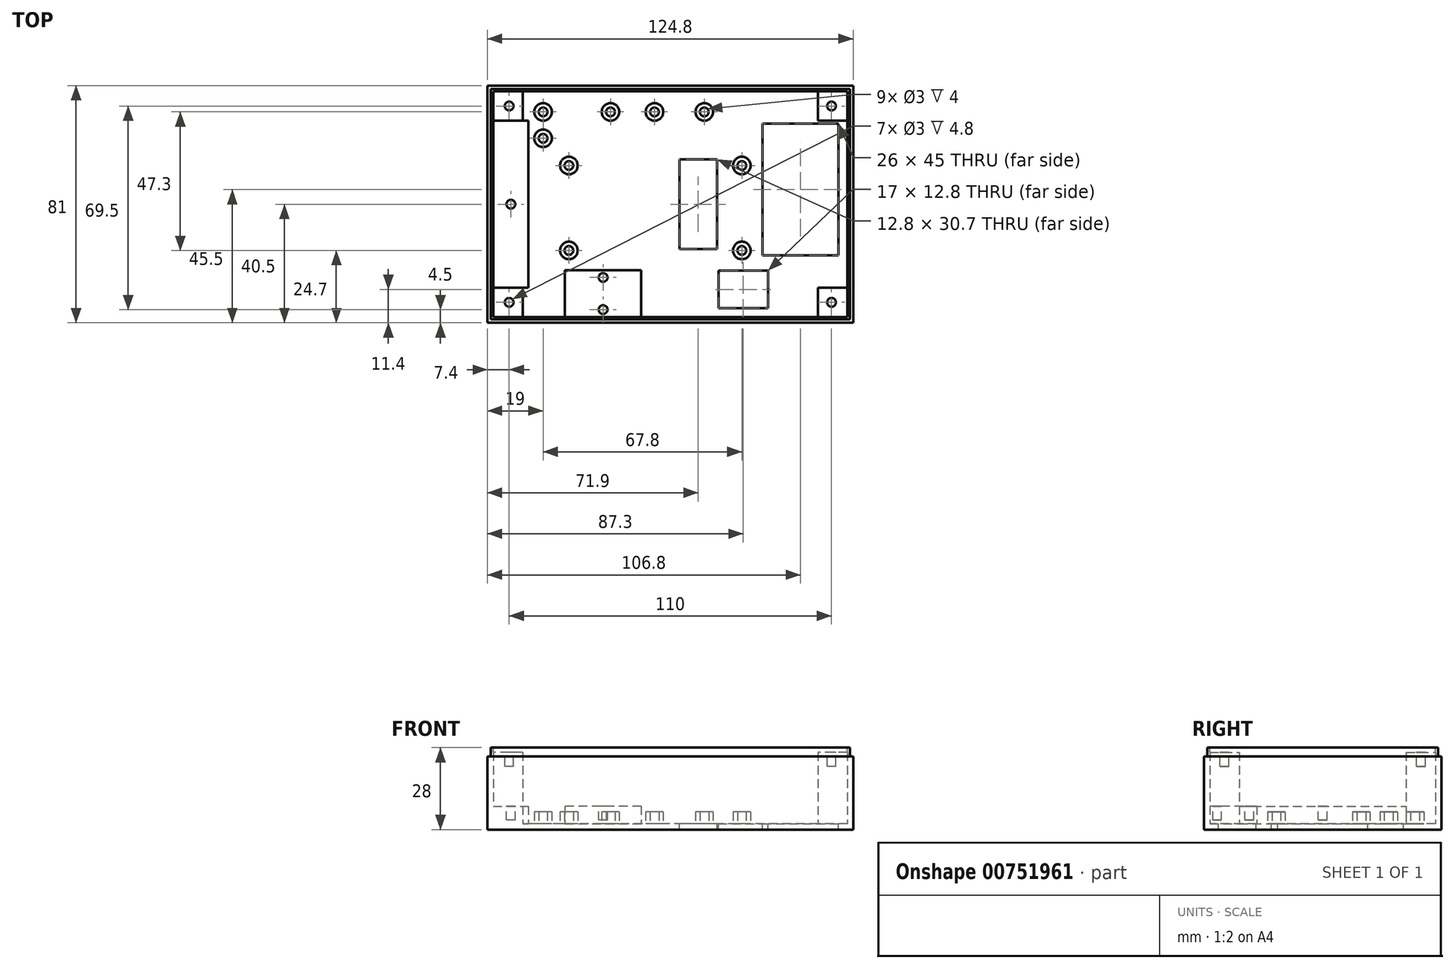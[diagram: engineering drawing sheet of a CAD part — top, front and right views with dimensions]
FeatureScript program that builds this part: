
annotation { "Feature Type Name" : "Feature", "Feature Type Description" : "" }
export const myFeature = defineFeature(function(context is Context, id is Id, definition is map)
    precondition{}
    {
        {
            var Q0;
            Q0=qCreatedBy(makeId("Top.planeOp"),FACE);
            var sketch = newSketch(context, id + "F0", { "sketchPlane" : qUnion([Q0])});
            skLineSegment(sketch, "E0.bottom", {"start": v(62.4, -40.5) * mm, "end": v(-62.4, -40.5) * mm});
            skLineSegment(sketch, "E0.top", {"start": v(62.4, 40.5) * mm, "end": v(-62.4, 40.5) * mm});
            skLineSegment(sketch, "E0.left", {"start": v(62.4, -40.5) * mm, "end": v(62.4, 40.5) * mm});
            skLineSegment(sketch, "E0.right", {"start": v(-62.4, -40.5) * mm, "end": v(-62.4, 40.5) * mm});
            skPoint(sketch, "E0.middle", {"position": v(0, 0) * mm});
            skSolve(sketch);
        }
        {
            var Q0;
            Q0 = qSketchRegion(id + "F0", true);
            extrude(context, id + "F1", {"entities" : qUnion([Q0]), "depth" : 25 * mm, "offsetDistance" : 25 * mm});
        }
        {
            var Q0;
            Q0=makeQuery(id+"F1.opExtrude","CAP_FACE",FACE,{"disambiguationData":[OSD([sQuery(id+"F0.wireOp",EDGE,"E0.bottom"),sQuery(id+"F0.wireOp",EDGE,"E0.top"),sQuery(id+"F0.wireOp",EDGE,"E0.left"),sQuery(id+"F0.wireOp",EDGE,"E0.right")])],"isStart":false});
            var sketch = newSketch(context, id + "F2", { "sketchPlane" : qUnion([Q0])});
            skLineSegment(sketch, "E1.bottom", {"start": v(61.25, -39.35) * mm, "end": v(-61.25, -39.35) * mm});
            skLineSegment(sketch, "E1.top", {"start": v(61.25, 39.35) * mm, "end": v(-61.25, 39.35) * mm});
            skLineSegment(sketch, "E1.left", {"start": v(61.25, -39.35) * mm, "end": v(61.25, 39.35) * mm});
            skLineSegment(sketch, "E1.right", {"start": v(-61.25, -39.35) * mm, "end": v(-61.25, 39.35) * mm});
            skPoint(sketch, "E1.middle", {"position": v(0, 0) * mm});
            skSolve(sketch);
        }
        {
            var Q0;
            Q0 = qSketchRegion(id + "F2", true);
            extrude(context, id + "F3", {"entities" : qUnion([Q0]), "operationType" : NewBodyOperationType.ADD, "depth" : 3 * mm, "offsetDistance" : 25 * mm});
        }
        {
            var Q0;
            Q0=makeQuery(id+"F3.opExtrude","CAP_FACE",FACE,{"disambiguationData":[OSD([sQuery(id+"F2.wireOp",EDGE,"E1.bottom"),sQuery(id+"F2.wireOp",EDGE,"E1.top"),sQuery(id+"F2.wireOp",EDGE,"E1.left"),sQuery(id+"F2.wireOp",EDGE,"E1.right")])],"isStart":false});
            var sketch = newSketch(context, id + "F4", { "sketchPlane" : qUnion([Q0])});
            skLineSegment(sketch, "E2.bottom", {"start": v(60.4, -38.5) * mm, "end": v(-60.4, -38.5) * mm});
            skLineSegment(sketch, "E2.top", {"start": v(60.4, 38.5) * mm, "end": v(-60.4, 38.5) * mm});
            skLineSegment(sketch, "E2.left", {"start": v(60.4, -38.5) * mm, "end": v(60.4, 38.5) * mm});
            skLineSegment(sketch, "E2.right", {"start": v(-60.4, -38.5) * mm, "end": v(-60.4, 38.5) * mm});
            skPoint(sketch, "E2.middle", {"position": v(0, 0) * mm});
            skSolve(sketch);
        }
        {
            var Q0;
            Q0 = qSketchRegion(id + "F4", true);
            extrude(context, id + "F5", {"entities" : qUnion([Q0]), "operationType" : NewBodyOperationType.REMOVE, "oppositeDirection" : true, "depth" : 26 * mm, "offsetDistance" : 25 * mm});
        }
        {
            var Q0;
            Q0=makeQuery(id+"F5.boolean.opBoolean","COPY",FACE,{"derivedFrom":makeQuery(id+"F5.opExtrude","CAP_FACE",FACE,{"disambiguationData":[OSD([sQuery(id+"F4.wireOp",EDGE,"E2.bottom"),sQuery(id+"F4.wireOp",EDGE,"E2.top"),sQuery(id+"F4.wireOp",EDGE,"E2.left"),sQuery(id+"F4.wireOp",EDGE,"E2.right")])],"isStart":false})});
            var sketch = newSketch(context, id + "F6", { "sketchPlane" : qUnion([Q0])});
            skLineSegment(sketch, "E3.bottom", {"start": v(-60.4, 38.5) * mm, "end": v(-50.4, 38.5) * mm});
            skLineSegment(sketch, "E3.top", {"start": v(-60.4, 28.5) * mm, "end": v(-50.4, 28.5) * mm});
            skLineSegment(sketch, "E3.left", {"start": v(-60.4, 38.5) * mm, "end": v(-60.4, 28.5) * mm});
            skLineSegment(sketch, "E3.right", {"start": v(-50.4, 38.5) * mm, "end": v(-50.4, 28.5) * mm});
            skLineSegment(sketch, "E4.bottom", {"start": v(-60.4, -38.5) * mm, "end": v(-50.4, -38.5) * mm});
            skLineSegment(sketch, "E4.top", {"start": v(-60.4, -28.5) * mm, "end": v(-50.4, -28.5) * mm});
            skLineSegment(sketch, "E4.left", {"start": v(-60.4, -38.5) * mm, "end": v(-60.4, -28.5) * mm});
            skLineSegment(sketch, "E4.right", {"start": v(-50.4, -38.5) * mm, "end": v(-50.4, -28.5) * mm});
            skLineSegment(sketch, "E5.bottom", {"start": v(60.4, -38.5) * mm, "end": v(50.4, -38.5) * mm});
            skLineSegment(sketch, "E5.top", {"start": v(60.4, -28.5) * mm, "end": v(50.4, -28.5) * mm});
            skLineSegment(sketch, "E5.left", {"start": v(60.4, -38.5) * mm, "end": v(60.4, -28.5) * mm});
            skLineSegment(sketch, "E5.right", {"start": v(50.4, -38.5) * mm, "end": v(50.4, -28.5) * mm});
            skLineSegment(sketch, "E6.bottom", {"start": v(60.4, 38.5) * mm, "end": v(50.4, 38.5) * mm});
            skLineSegment(sketch, "E6.top", {"start": v(60.4, 28.5) * mm, "end": v(50.4, 28.5) * mm});
            skLineSegment(sketch, "E6.left", {"start": v(60.4, 38.5) * mm, "end": v(60.4, 28.5) * mm});
            skLineSegment(sketch, "E6.right", {"start": v(50.4, 38.5) * mm, "end": v(50.4, 28.5) * mm});
            skSolve(sketch);
        }
        {
            var Q0;
            Q0 = qSketchRegion(id + "F6", true);
            extrude(context, id + "F7", {"entities" : qUnion([Q0]), "operationType" : NewBodyOperationType.ADD, "depth" : 24.4 * mm, "offsetDistance" : 25 * mm});
        }
        {
            var Q0;
            Q0=makeQuery(id+"F7.opExtrude","CAP_FACE",FACE,{"disambiguationData":[OSD([sQuery(id+"F6.wireOp",EDGE,"E3.bottom"),sQuery(id+"F6.wireOp",EDGE,"E3.top"),sQuery(id+"F6.wireOp",EDGE,"E3.left"),sQuery(id+"F6.wireOp",EDGE,"E3.right")])],"isStart":false});
            var sketch = newSketch(context, id + "F8", { "sketchPlane" : qUnion([Q0])});
            skCircle(sketch, "E7", {"center": v(-55, 33.5) * mm, "radius": 1.5 * mm});
            skPoint(sketch, "E7.centerSnap0", {"position": v(-50.4, 33.5) * mm});
            skCircle(sketch, "E8", {"center": v(-55, -33.5) * mm, "radius": 1.5 * mm});
            skCircle(sketch, "E9", {"center": v(55, -33.5) * mm, "radius": 1.5 * mm});
            skCircle(sketch, "E10", {"center": v(55, 33.5) * mm, "radius": 1.5 * mm});
            skSolve(sketch);
        }
        {
            var Q0;
            Q0 = qSketchRegion(id + "F8", true);
            extrude(context, id + "F9", {"entities" : qUnion([Q0]), "operationType" : NewBodyOperationType.REMOVE, "oppositeDirection" : true, "depth" : 4.8 * mm, "offsetDistance" : 25 * mm});
        }
        {
            var Q0;
            Q0=makeQuery(id+"F5.boolean.opBoolean","COPY",FACE,{"derivedFrom":makeQuery(id+"F5.opExtrude","CAP_FACE",FACE,{"disambiguationData":[OSD([sQuery(id+"F4.wireOp",EDGE,"E2.bottom"),sQuery(id+"F4.wireOp",EDGE,"E2.top"),sQuery(id+"F4.wireOp",EDGE,"E2.left"),sQuery(id+"F4.wireOp",EDGE,"E2.right")])],"isStart":false})});
            var sketch = newSketch(context, id + "F10", { "sketchPlane" : qUnion([Q0])});
            skLineSegment(sketch, "E11.bottom", {"start": v(31.4, 27.5) * mm, "end": v(57.4, 27.5) * mm});
            skLineSegment(sketch, "E11.top", {"start": v(31.4, -17.5) * mm, "end": v(57.4, -17.5) * mm});
            skLineSegment(sketch, "E11.left", {"start": v(31.4, 27.5) * mm, "end": v(31.4, -17.5) * mm});
            skLineSegment(sketch, "E11.right", {"start": v(57.4, 27.5) * mm, "end": v(57.4, -17.5) * mm});
            skLineSegment(sketch, "E12.bottom", {"start": v(16.4, -22.7) * mm, "end": v(33.4, -22.7) * mm});
            skLineSegment(sketch, "E12.top", {"start": v(16.4, -35.5) * mm, "end": v(33.4, -35.5) * mm});
            skLineSegment(sketch, "E12.left", {"start": v(16.4, -22.7) * mm, "end": v(16.4, -35.5) * mm});
            skLineSegment(sketch, "E12.right", {"start": v(33.4, -22.7) * mm, "end": v(33.4, -35.5) * mm});
            skLineSegment(sketch, "E13.bottom", {"start": v(15.9, -15.35) * mm, "end": v(3.1, -15.35) * mm});
            skLineSegment(sketch, "E13.top", {"start": v(15.9, 15.35) * mm, "end": v(3.1, 15.35) * mm});
            skLineSegment(sketch, "E13.left", {"start": v(15.9, -15.35) * mm, "end": v(15.9, 15.35) * mm});
            skLineSegment(sketch, "E13.right", {"start": v(3.1, -15.35) * mm, "end": v(3.1, 15.35) * mm});
            skPoint(sketch, "E13.middle", {"position": v(9.5, 0) * mm});
            skSolve(sketch);
        }
        {
            var Q0;
            Q0 = qSketchRegion(id + "F10", true);
            extrude(context, id + "F11", {"entities" : qUnion([Q0]), "operationType" : NewBodyOperationType.REMOVE, "endBound" : BoundingType.THROUGH_ALL, "oppositeDirection" : true, "depth" : 25 * mm, "offsetDistance" : 25 * mm});
        }
        {
            var Q0;
            Q0=makeQuery(id+"F5.boolean.opBoolean","COPY",FACE,{"derivedFrom":makeQuery(id+"F5.opExtrude","CAP_FACE",FACE,{"disambiguationData":[OSD([sQuery(id+"F4.wireOp",EDGE,"E2.bottom"),sQuery(id+"F4.wireOp",EDGE,"E2.top"),sQuery(id+"F4.wireOp",EDGE,"E2.left"),sQuery(id+"F4.wireOp",EDGE,"E2.right")])],"isStart":false})});
            var sketch = newSketch(context, id + "F12", { "sketchPlane" : qUnion([Q0])});
            skCircle(sketch, "E14", {"center": v(24.4, 13.2) * mm, "radius": 3 * mm});
            skCircle(sketch, "E15", {"center": v(-34.6, 13.2) * mm, "radius": 3 * mm});
            skCircle(sketch, "E16", {"center": v(-34.6, -15.8) * mm, "radius": 3 * mm});
            skCircle(sketch, "E17", {"center": v(24.4, -15.8) * mm, "radius": 3 * mm});
            skCircle(sketch, "E18", {"center": v(-43.4, 31.5) * mm, "radius": 3 * mm});
            skCircle(sketch, "E19", {"center": v(-43.4, 22.5) * mm, "radius": 3 * mm});
            skCircle(sketch, "E20", {"center": v(-20.4, 31.5) * mm, "radius": 3 * mm});
            skCircle(sketch, "E21", {"center": v(-5.4, 31.5) * mm, "radius": 3 * mm});
            skCircle(sketch, "E22", {"center": v(11.6, 31.5) * mm, "radius": 3 * mm});
            skSolve(sketch);
        }
        {
            var Q0;
            Q0 = qSketchRegion(id + "F12", true);
            extrude(context, id + "F13", {"entities" : qUnion([Q0]), "operationType" : NewBodyOperationType.ADD, "depth" : 4 * mm, "offsetDistance" : 25 * mm});
        }
        {
            var Q0;
            Q0=makeQuery(id+"F5.boolean.opBoolean","COPY",FACE,{"derivedFrom":makeQuery(id+"F5.opExtrude","CAP_FACE",FACE,{"disambiguationData":[OSD([sQuery(id+"F4.wireOp",EDGE,"E2.bottom"),sQuery(id+"F4.wireOp",EDGE,"E2.top"),sQuery(id+"F4.wireOp",EDGE,"E2.left"),sQuery(id+"F4.wireOp",EDGE,"E2.right")])],"isStart":false})});
            var sketch = newSketch(context, id + "F14", { "sketchPlane" : qUnion([Q0])});
            skCircle(sketch, "E23", {"center": v(-34.6, -15.8) * mm, "radius": 1.5 * mm});
            skCircle(sketch, "E24", {"center": v(24.4, -15.8) * mm, "radius": 1.5 * mm});
            skCircle(sketch, "E25", {"center": v(-34.6, 13.2) * mm, "radius": 1.5 * mm});
            skCircle(sketch, "E26", {"center": v(24.4, 13.2) * mm, "radius": 1.5 * mm});
            skCircle(sketch, "E27", {"center": v(11.6, 31.5) * mm, "radius": 1.5 * mm});
            skCircle(sketch, "E28", {"center": v(-5.4, 31.5) * mm, "radius": 1.5 * mm});
            skCircle(sketch, "E29", {"center": v(-20.4, 31.5) * mm, "radius": 1.5 * mm});
            skCircle(sketch, "E30", {"center": v(-43.4, 22.5) * mm, "radius": 1.5 * mm});
            skCircle(sketch, "E31", {"center": v(-43.4, 31.5) * mm, "radius": 1.5 * mm});
            skSolve(sketch);
        }
        {
            var Q0;
            Q0 = qSketchRegion(id + "F14", true);
            extrude(context, id + "F15", {"entities" : qUnion([Q0]), "operationType" : NewBodyOperationType.REMOVE, "depth" : 4.8 * mm, "offsetDistance" : 25 * mm});
        }
        {
            var Q0;
            Q0=makeQuery(id+"F5.boolean.opBoolean","COPY",FACE,{"derivedFrom":makeQuery(id+"F5.opExtrude","CAP_FACE",FACE,{"disambiguationData":[OSD([sQuery(id+"F4.wireOp",EDGE,"E2.bottom"),sQuery(id+"F4.wireOp",EDGE,"E2.top"),sQuery(id+"F4.wireOp",EDGE,"E2.left"),sQuery(id+"F4.wireOp",EDGE,"E2.right")])],"isStart":false})});
            var sketch = newSketch(context, id + "F16", { "sketchPlane" : qUnion([Q0])});
            skLineSegment(sketch, "E32.bottom", {"start": v(-60.4, -28.5) * mm, "end": v(-48.4, -28.5) * mm});
            skLineSegment(sketch, "E32.top", {"start": v(-60.4, 28.5) * mm, "end": v(-48.4, 28.5) * mm});
            skLineSegment(sketch, "E32.left", {"start": v(-60.4, -28.5) * mm, "end": v(-60.4, 28.5) * mm});
            skLineSegment(sketch, "E32.right", {"start": v(-48.4, -28.5) * mm, "end": v(-48.4, 28.5) * mm});
            skSolve(sketch);
        }
        {
            var Q0;
            Q0 = qSketchRegion(id + "F16", true);
            extrude(context, id + "F17", {"entities" : qUnion([Q0]), "operationType" : NewBodyOperationType.ADD, "depth" : 6 * mm, "offsetDistance" : 25 * mm});
        }
        {
            var Q0;
            Q0=makeQuery(id+"F17.opExtrude","CAP_FACE",FACE,{"disambiguationData":[OSD([sQuery(id+"F16.wireOp",EDGE,"E32.bottom"),sQuery(id+"F16.wireOp",EDGE,"E32.top"),sQuery(id+"F16.wireOp",EDGE,"E32.left"),sQuery(id+"F16.wireOp",EDGE,"E32.right")])],"isStart":false});
            var sketch = newSketch(context, id + "F18", { "sketchPlane" : qUnion([Q0])});
            skCircle(sketch, "E33", {"center": v(-54.4, 0) * mm, "radius": 1.5 * mm});
            skPoint(sketch, "E33.centerSnap0", {"position": v(-48.4, 0) * mm});
            skSolve(sketch);
        }
        {
            var Q0;
            Q0 = qSketchRegion(id + "F18", true);
            extrude(context, id + "F19", {"entities" : qUnion([Q0]), "operationType" : NewBodyOperationType.REMOVE, "oppositeDirection" : true, "depth" : 4.8 * mm, "offsetDistance" : 25 * mm});
        }
        {
            var Q0;
            Q0=makeQuery(id+"F5.boolean.opBoolean","COPY",FACE,{"derivedFrom":makeQuery(id+"F5.opExtrude","CAP_FACE",FACE,{"disambiguationData":[OSD([sQuery(id+"F4.wireOp",EDGE,"E2.bottom"),sQuery(id+"F4.wireOp",EDGE,"E2.top"),sQuery(id+"F4.wireOp",EDGE,"E2.left"),sQuery(id+"F4.wireOp",EDGE,"E2.right")])],"isStart":false})});
            var sketch = newSketch(context, id + "F20", { "sketchPlane" : qUnion([Q0])});
            skLineSegment(sketch, "E34.bottom", {"start": v(-35.93, -22.5) * mm, "end": v(-9.93, -22.5) * mm});
            skLineSegment(sketch, "E34.top", {"start": v(-35.93, -38.5) * mm, "end": v(-9.93, -38.5) * mm});
            skLineSegment(sketch, "E34.left", {"start": v(-35.93, -22.5) * mm, "end": v(-35.93, -38.5) * mm});
            skLineSegment(sketch, "E34.right", {"start": v(-9.93, -22.5) * mm, "end": v(-9.93, -38.5) * mm});
            skSolve(sketch);
        }
        {
            var Q0;
            Q0 = qSketchRegion(id + "F20", true);
            extrude(context, id + "F21", {"entities" : qUnion([Q0]), "operationType" : NewBodyOperationType.ADD, "depth" : 6 * mm, "offsetDistance" : 25 * mm});
        }
        {
            var Q0;
            Q0=makeQuery(id+"F21.opExtrude","CAP_FACE",FACE,{"disambiguationData":[OSD([sQuery(id+"F20.wireOp",EDGE,"E34.bottom"),sQuery(id+"F20.wireOp",EDGE,"E34.top"),sQuery(id+"F20.wireOp",EDGE,"E34.left"),sQuery(id+"F20.wireOp",EDGE,"E34.right")])],"isStart":false});
            var sketch = newSketch(context, id + "F22", { "sketchPlane" : qUnion([Q0])});
            skCircle(sketch, "E35", {"center": v(-22.93, -25) * mm, "radius": 1.5 * mm});
            skPoint(sketch, "E35.centerSnap0", {"position": v(-22.93, -22.5) * mm});
            skPoint(sketch, "E35.perimeterSnap0", {"position": v(-22.93, -22.5) * mm});
            skPoint(sketch, "E35.perimeterSnap1", {"position": v(-35.93, -30.5) * mm});
            skCircle(sketch, "E36", {"center": v(-22.93, -36) * mm, "radius": 1.5 * mm});
            skSolve(sketch);
        }
        {
            var Q0;
            Q0 = qSketchRegion(id + "F22", true);
            extrude(context, id + "F23", {"entities" : qUnion([Q0]), "operationType" : NewBodyOperationType.REMOVE, "oppositeDirection" : true, "depth" : 4.8 * mm, "offsetDistance" : 25 * mm});
        }
    });
